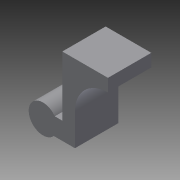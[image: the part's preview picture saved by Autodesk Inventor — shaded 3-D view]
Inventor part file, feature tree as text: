
AUTODESK INVENTOR PART (.ipt)
format: ipt  version: 2015 (Build 190159000, 159)  size: 176,640 bytes
history: native  units: in
note: dims shown in document units (in); Inventor stores cm internally (conversion verified against a paired STEP export)
features: extrude x10, sketch x10, projected_geometry x4, mirror x2, reference x2, fillet x1
ambient origin geometry x8: Origin, YZ Plane, XZ Plane, XY Plane, X Axis, Y Axis, Z Axis, Center Point
bodies: Solid1 (feature_tree)
feature tree (29):
  extrude  "Extrusion1"  Depth=0.9375in TaperAngle=0.0deg
  extrude  "Extrusion2"  Depth=0.4882in TaperAngle=0.0deg
  mirror  "Mirror1"
  extrude  "Extrusion3"  Depth=0.4331in TaperAngle=0.0deg
  extrude  "Extrusion4"  Depth=0.3831in
  mirror  "Mirror2"
  extrude  "Extrusion5"  Depth=1.0in
  fillet  "Fillet3"  Radius=1.0in
  extrude  "Extrusion6"  Depth=0.216in TaperAngle=0.0deg
  extrude  "Extrusion7"  Depth=0.216in TaperAngle=0.0deg
  extrude  "Extrusion8"  [1 undecoded]
  extrude  "Extrusion9"  [1 undecoded]
  extrude  "Extrusion10"  [1 undecoded]
  sketch  "Sketch1"  dims[d0=0.375in d1=0.0in d2=0.9375in d3=0.0in]
  reference  "Reference1"
  sketch  "Sketch2"  dims[d4=0.3125in d5=0.4882in d6=0.0in]
  sketch  "Sketch3"  dims[d7=0.4331in d8=0.0591in d9=0.0in]
  sketch  "Sketch4"  dims[d11=2.3455in d12=0.3831in]
  sketch  "Sketch7"  dims[d13=1.0in d14=0.0in d16=1.0in d17=1.0in d18=0.0in]
  projected_geometry  "Projected Loop1"
  sketch  "Sketch9"  dims[d19=1.0in d20=0.0in d21=0.216in d22=0.0in]
  projected_geometry  "Projected Loop2"
  sketch  "Sketch10"  dims[d23=0.25in d24=0.216in d25=0.0in]
  sketch  "Sketch11"  dims[d26=0.216in d27=0.0in]
  reference  "Reference2"
  sketch  "Sketch12"
  sketch  "Sketch13"
  projected_geometry  "Projected Loop3"
  projected_geometry  "Projected Loop4"
note: 3 required parameter values undecoded (feature->parameter linkage not recoverable at this tier; creation-order binding heuristic only, values carry confidence <= 0.55)
